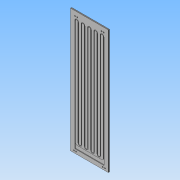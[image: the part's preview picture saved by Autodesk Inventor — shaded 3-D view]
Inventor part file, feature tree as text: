
AUTODESK INVENTOR PART (.ipt)
format: ipt  version: 2013 (Build 170138000, 138)  size: 247,296 bytes
history: native  units: in
note: dims shown in document units (in); Inventor stores cm internally (conversion verified against a paired STEP export)
features: other x11, extrude x2, hole x1
ambient origin geometry x8: Origin, YZ Plane, XZ Plane, XY Plane, X Axis, Y Axis, Z Axis, Center Point
bodies: Solid1 (feature_tree)
feature tree (14):
  other  "Blocks"
  extrude  "Stck Extrusion"  Depth=23.8125in
  extrude  "Extrusion3"  Depth=78.0in
  other  "Side profile reference"
  hole  "Hole1"  [1 undecoded]
  other  "Stock"
  other  "LEDPocket"
  other  "TwoLineColumn"
  other  "TwoLineColumnEnd"
  other  "15mm Neon profile"
  other  "U Bolt hole and bore"
  other  "U-Bolt holes"
  other  "15mm Neon profile:1"
  other  "15mm Neon profile:2"
note: 1 required parameter value undecoded (feature->parameter linkage not recoverable at this tier; creation-order binding heuristic only, values carry confidence <= 0.55)
